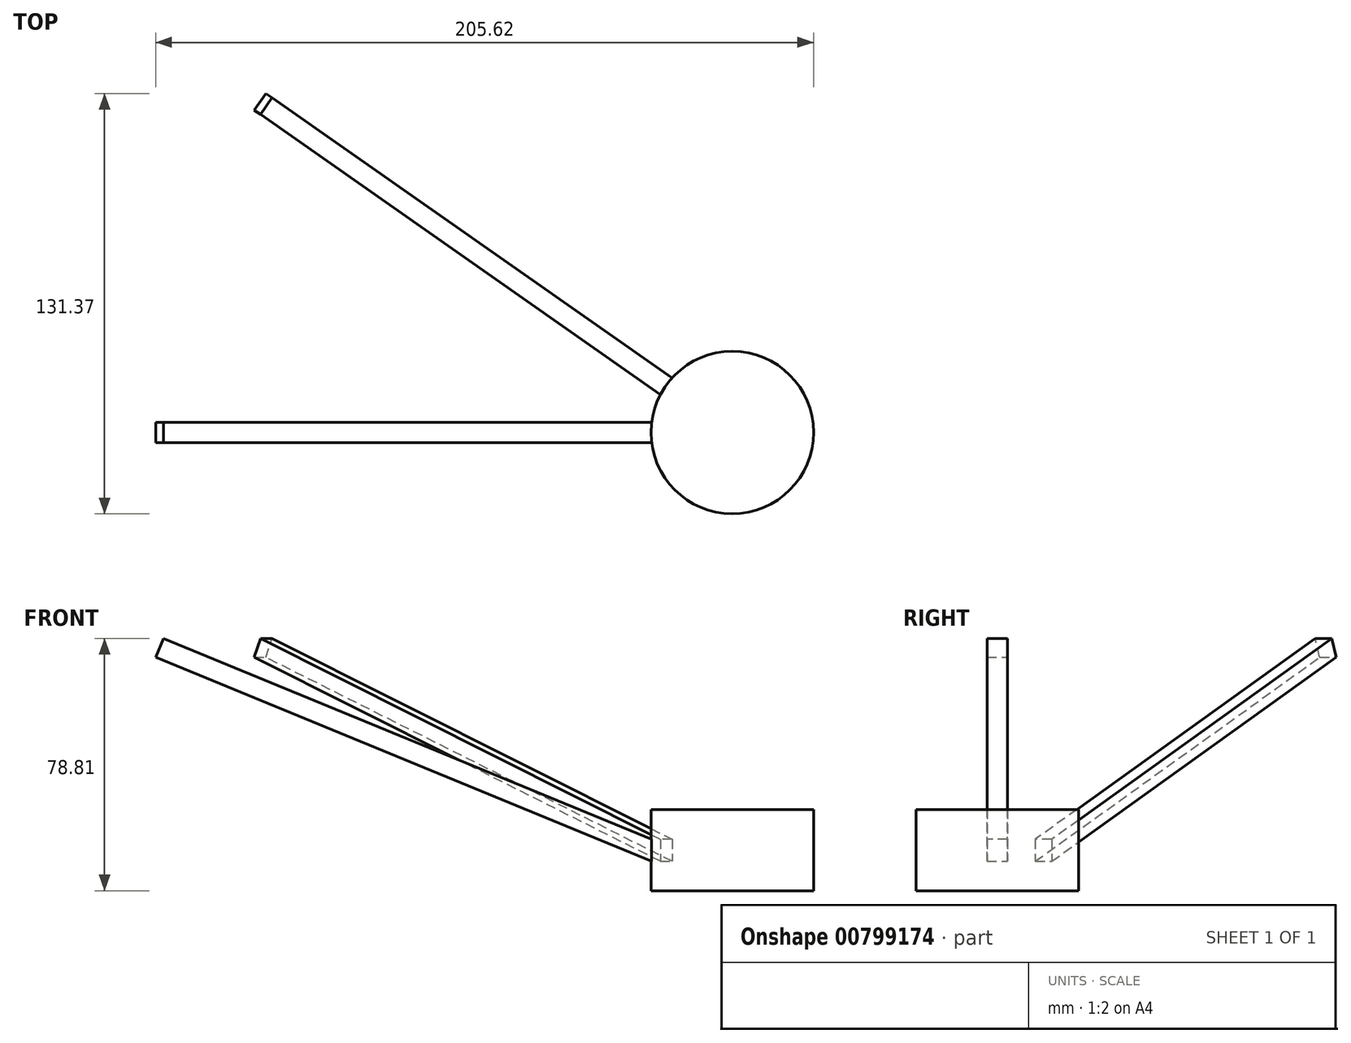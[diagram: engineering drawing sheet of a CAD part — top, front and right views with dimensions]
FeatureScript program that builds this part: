
annotation { "Feature Type Name" : "Feature", "Feature Type Description" : "" }
export const myFeature = defineFeature(function(context is Context, id is Id, definition is map)
    precondition{}
    {
        {
            var Q0;
            Q0=qCreatedBy(makeId("Top.planeOp"),FACE);
            var sketch = newSketch(context, id + "F0", { "sketchPlane" : qUnion([Q0])});
            skCircle(sketch, "E0", {"center": v(0, 0) * mm, "radius": 25.4 * mm});
            skSolve(sketch);
        }
        {
            var Q0;
            Q0=qSketchRegion(id+"F0",true);
            extrude(context, id + "F1", {"entities" : qUnion([Q0]), "endBound" : BoundingType.SYMMETRIC, "depth" : 25.4 * mm});
        }
        {
            var Q0;
            Q0=qCreatedBy(makeId("Front.planeOp"),FACE);
            var sketch = newSketch(context, id + "F2", { "sketchPlane" : qUnion([Q0])});
            skLineSegment(sketch, "E1", {"start": v(-25.4, -3.43) * mm, "end": v(-180.22, 60.23) * mm});
            skLineSegment(sketch, "E2", {"start": v(-180.22, 60.23) * mm, "end": v(-177.8, 66.1) * mm});
            skLineSegment(sketch, "E3", {"start": v(-177.8, 66.1) * mm, "end": v(-25.4, 3.43) * mm});
            skLineSegment(sketch, "E4", {"start": v(-25.4, 12.7) * mm, "end": v(-25.4, 3.43) * mm, "construction": true});
            skLineSegment(sketch, "E5", {"start": v(-25.4, 3.43) * mm, "end": v(-16.93, -0.05) * mm});
            skLineSegment(sketch, "E6", {"start": v(-16.93, -0.05) * mm, "end": v(-19.35, -5.92) * mm});
            skLineSegment(sketch, "E7", {"start": v(-19.35, -5.92) * mm, "end": v(-25.4, -3.43) * mm});
            skLineSegment(sketch, "E8", {"start": v(-25.4, -12.7) * mm, "end": v(-25.4, -3.43) * mm, "construction": true});
            skLineSegment(sketch, "E9", {"start": v(-25.4, 3.43) * mm, "end": v(-16.93, 3.43) * mm, "construction": true});
            skLineSegment(sketch, "E10", {"start": v(-16.93, 3.43) * mm, "end": v(-8.47, 3.43) * mm, "construction": true});
            skLineSegment(sketch, "E11", {"start": v(-8.47, 3.43) * mm, "end": v(0, 3.43) * mm, "construction": true});
            skSolve(sketch);
        }
        {
            var Q0;
            Q0=qSketchRegion(id+"F2",true);
            extrude(context, id + "F3", {"entities" : qUnion([Q0]), "operationType" : NewBodyOperationType.ADD, "endBound" : BoundingType.SYMMETRIC, "depth" : 6.35 * mm});
        }
        {
            var Q0;
            Q0=makeQuery(id+"F3.opExtrude","SWEPT_FACE",FACE,{"disambiguationData":[OSD([sQuery(id+"F2.wireOp",EDGE,"E3"),sQuery(id+"F2.wireOp",EDGE,"E5")])]});
            var Q1;
            Q1=makeQuery(id+"F3.opExtrude","CAP_FACE",FACE,{"disambiguationData":[OSD([sQuery(id+"F2.wireOp",EDGE,"E1"),sQuery(id+"F2.wireOp",EDGE,"E2"),sQuery(id+"F2.wireOp",EDGE,"E3"),sQuery(id+"F2.wireOp",EDGE,"E5"),sQuery(id+"F2.wireOp",EDGE,"E6"),sQuery(id+"F2.wireOp",EDGE,"E7")])],"isStart":false});
            var Q2;
            Q2=makeQuery(id+"F3.opExtrude","SWEPT_FACE",FACE,{"disambiguationData":[OSD([sQuery(id+"F2.wireOp",EDGE,"E2")])]});
            var Q3;
            Q3=makeQuery(id+"F3.opExtrude","SWEPT_FACE",FACE,{"disambiguationData":[OSD([sQuery(id+"F2.wireOp",EDGE,"E1"),sQuery(id+"F2.wireOp",EDGE,"E7")])]});
            var Q4;
            Q4=makeQuery(id+"F3.opExtrude","CAP_FACE",FACE,{"disambiguationData":[OSD([sQuery(id+"F2.wireOp",EDGE,"E1"),sQuery(id+"F2.wireOp",EDGE,"E2"),sQuery(id+"F2.wireOp",EDGE,"E3"),sQuery(id+"F2.wireOp",EDGE,"E5"),sQuery(id+"F2.wireOp",EDGE,"E6"),sQuery(id+"F2.wireOp",EDGE,"E7")])],"isStart":true});
            var Q5;
            Q5=makeQuery(id+"F1.opExtrude","SWEPT_FACE",FACE,{"disambiguationData":[OSD([sQuery(id+"F0.wireOp",EDGE,"E0")])]});
            circularPattern(context, id + "F4", {"faces" : qUnion([Q0, Q1, Q2, Q3, Q4]), "axis" : qUnion([Q5]), "angle" : 35 * degree, "instanceCount" : 2, "patternType" : PatternType.FACE});
        }
    });
